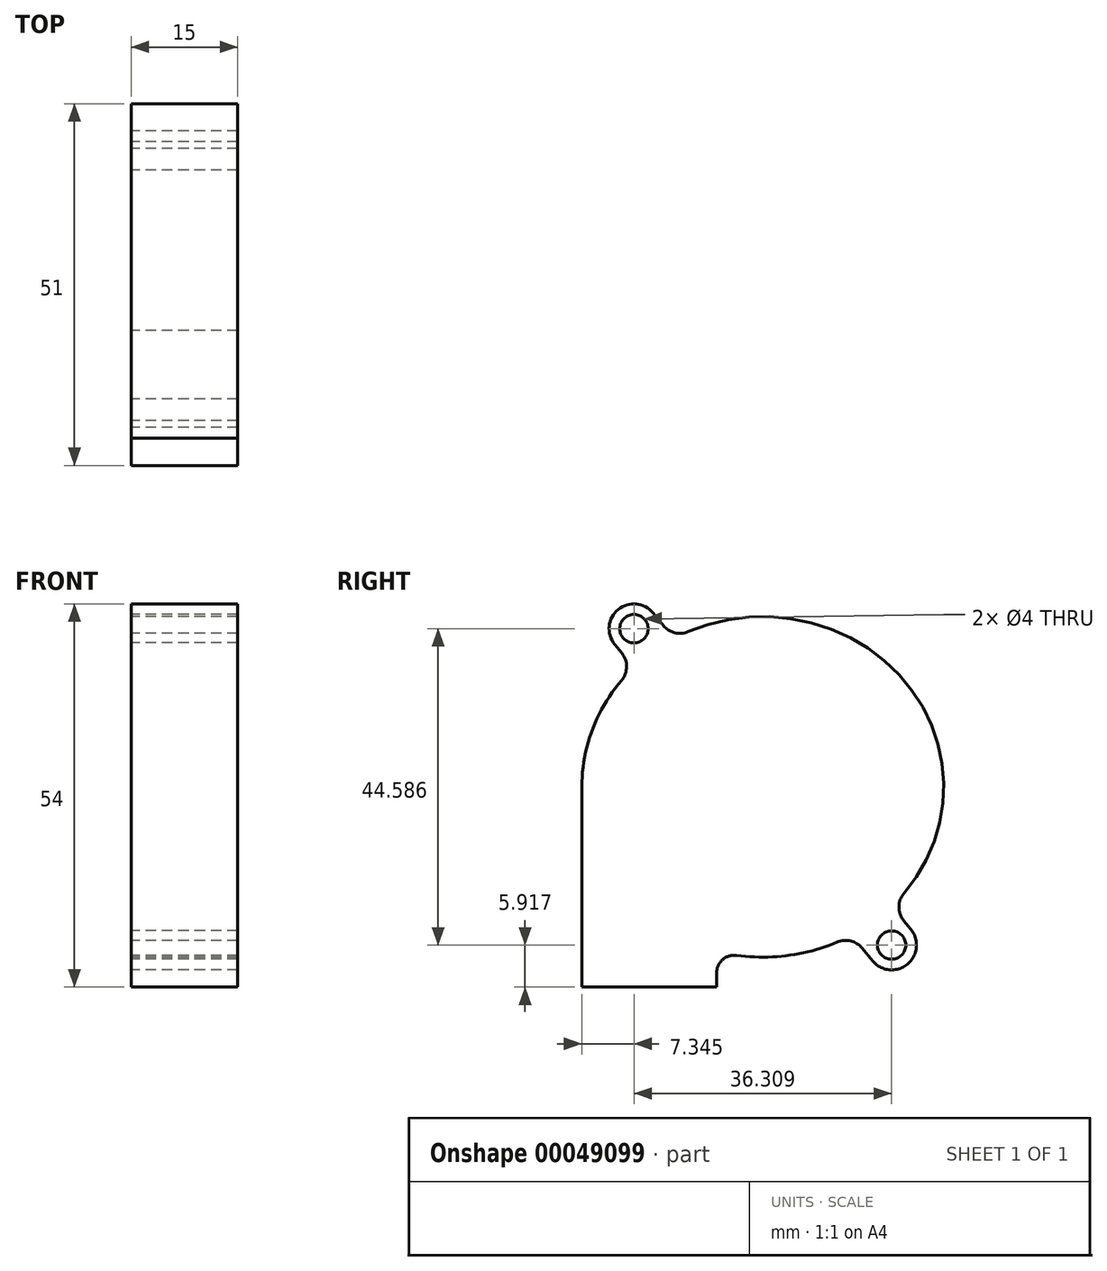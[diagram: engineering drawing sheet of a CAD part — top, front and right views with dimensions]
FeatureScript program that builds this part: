
annotation { "Feature Type Name" : "Feature", "Feature Type Description" : "" }
export const myFeature = defineFeature(function(context is Context, id is Id, definition is map)
    precondition{}
    {
        {
            var Q0;
            Q0=qCreatedBy(makeId("Right.planeOp"),FACE);
            var sketch = newSketch(context, id + "F0", { "sketchPlane" : qUnion([Q0])});
            skEllipticalArc(sketch, "E0", {});
            skLineSegment(sketch, "E1", {"start": v(-25.5, 0) * mm, "end": v(-25.5, -28.2) * mm});
            skLineSegment(sketch, "E2", {"start": v(-25.5, -28.2) * mm, "end": v(-6.5, -28.2) * mm});
            skLineSegment(sketch, "E3", {"start": v(-6.5, -28.2) * mm, "end": v(-6.5, -26.2) * mm});
            skPoint(sketch, "E4.visualSharp", {"position": v(-25.5, -28.2) * mm});
            skPoint(sketch, "E5.visualSharp", {"position": v(-6.5, -23.2) * mm});
            skArc(sketch, "E5.filletArc", {"start": v(-3.68, -23.75) * mm, "mid": v(-5.65, -24.34) * mm, "end": v(-6.5, -26.2) * mm});
            skCircle(sketch, "E6", {"center": v(-18.15, 22.3) * mm, "radius": 2 * mm});
            skCircle(sketch, "E7", {"center": v(18.15, -22.3) * mm, "radius": 2 * mm});
            skLineSegment(sketch, "E8", {"start": v(-18.15, 22.3) * mm, "end": v(-15.51, 19.05) * mm});
            skPoint(sketch, "E9", {"position": v(-15.51, 19.05) * mm});
            skPoint(sketch, "E10", {"position": v(15.51, -19.05) * mm});
            skLineSegment(sketch, "E11.trimOffspring", {"start": v(15.51, -19.05) * mm, "end": v(18.15, -22.3) * mm});
            skArc(sketch, "E12", {"start": v(-15.44, 24.5) * mm, "mid": v(-20.36, 25) * mm, "end": v(-20.87, 20.08) * mm});
            skArc(sketch, "E13", {"start": v(15.44, -24.5) * mm, "mid": v(20.36, -25) * mm, "end": v(20.87, -20.08) * mm});
            skLineSegment(sketch, "E14", {"start": v(-15.44, 24.5) * mm, "end": v(-14, 22.74) * mm});
            skLineSegment(sketch, "E15", {"start": v(15.44, -24.5) * mm, "end": v(14, -22.74) * mm});
            skEllipticalArc(sketch, "E16.trimOffspring", {});
            skEllipticalArc(sketch, "E17.trimOffspring", {});
            skLineSegment(sketch, "E18.trimOffspring", {"start": v(-19.86, 18.84) * mm, "end": v(-20.87, 20.08) * mm});
            skLineSegment(sketch, "E19.trimOffspring", {"start": v(19.86, -18.84) * mm, "end": v(20.87, -20.08) * mm});
            skPoint(sketch, "E20.visualSharp", {"position": v(-12.52, 20.91) * mm});
            skArc(sketch, "E20.filletArc", {"start": v(-14, 22.74) * mm, "mid": v(-12.4, 21.72) * mm, "end": v(-10.5, 21.87) * mm});
            skPoint(sketch, "E21.visualSharp", {"position": v(-18.2, 16.8) * mm});
            skArc(sketch, "E21.filletArc", {"start": v(-19.9, 15) * mm, "mid": v(-19.19, 16.92) * mm, "end": v(-19.86, 18.84) * mm});
            skPoint(sketch, "E22.visualSharp", {"position": v(18.2, -16.8) * mm});
            skArc(sketch, "E22.filletArc", {"start": v(19.9, -15) * mm, "mid": v(19.19, -16.92) * mm, "end": v(19.86, -18.84) * mm});
            skPoint(sketch, "E23.visualSharp", {"position": v(12.52, -20.91) * mm});
            skArc(sketch, "E23.filletArc", {"start": v(14, -22.74) * mm, "mid": v(12.4, -21.72) * mm, "end": v(10.5, -21.87) * mm});
            const initialGuessF0  = {"E0": [0, 0, 1, 0, 0.0255, 0.024, 4.56753628514583, 5.1368548975140955], "E16.trimOffspring": [0, 0, 1, 0, 0.0255, 0.024, 2.4661882520020417, 3.141592653589793], "E17.trimOffspring": [0, 0, 1, 0, 0.0255, 0.024, 5.607780905591834, 1.9952622439243024]};
            skSetInitialGuess(sketch, initialGuessF0);
            skSolve(sketch);
        }
        {
            var Q0;
            Q0 = qSketchRegion(id + "F0", true);
            extrude(context, id + "F1", {"entities" : qUnion([Q0]), "depth" : 15 * mm});
        }
    });
